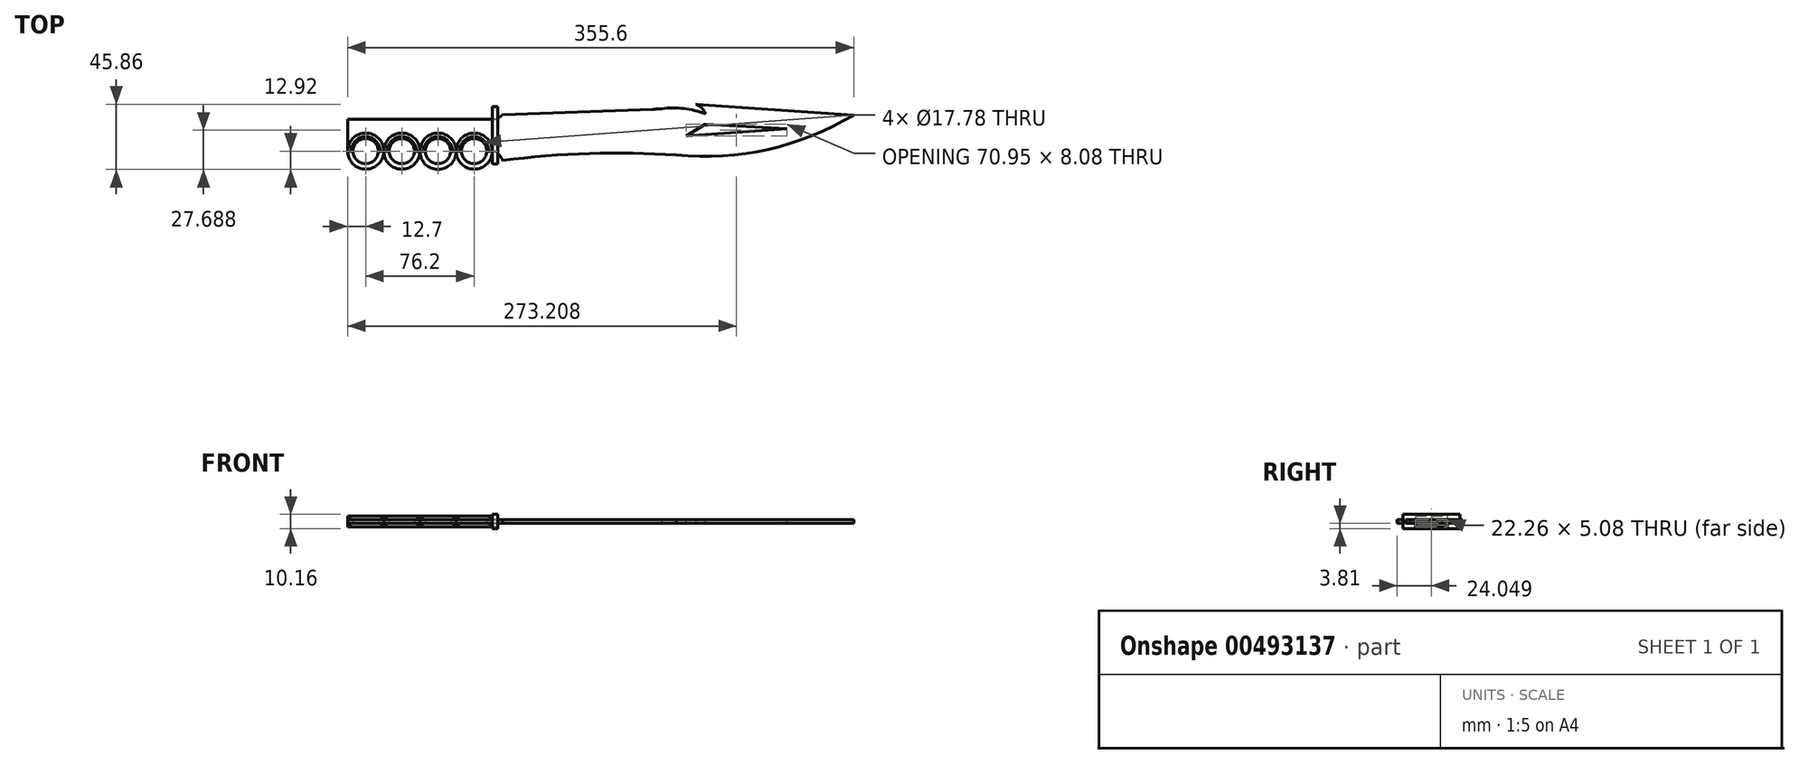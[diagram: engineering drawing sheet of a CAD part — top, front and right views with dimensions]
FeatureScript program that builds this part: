
annotation { "Feature Type Name" : "Feature", "Feature Type Description" : "" }
export const myFeature = defineFeature(function(context is Context, id is Id, definition is map)
    precondition{}
    {
        {
            var Q0;
            Q0=qCreatedBy(makeId("Top.planeOp"),FACE);
            var sketch = newSketch(context, id + "F0", { "sketchPlane" : qUnion([Q0])});
            skLineSegment(sketch, "E0.left", {"start": v(0, 0) * mm, "end": v(0, 22.26) * mm});
            skLineSegment(sketch, "E0.right", {"start": v(-101.6, 0) * mm, "end": v(-101.6, 22.26) * mm});
            skCircle(sketch, "E1", {"center": v(-88.9, 0) * mm, "radius": 8.9 * mm});
            skCircle(sketch, "E2", {"center": v(-63.5, 0) * mm, "radius": 8.9 * mm});
            skCircle(sketch, "E3", {"center": v(-38.1, 0) * mm, "radius": 8.9 * mm});
            skCircle(sketch, "E4", {"center": v(-12.7, 0) * mm, "radius": 8.9 * mm});
            skArc(sketch, "E5", {"start": v(-66.76, 22.26) * mm, "mid": v(-50.8, 21.91) * mm, "end": v(-34.84, 22.26) * mm});
            skPoint(sketch, "E6", {"position": v(-76.2, 0) * mm});
            skPoint(sketch, "E7", {"position": v(-50.8, 0) * mm});
            skPoint(sketch, "E8", {"position": v(-25.4, 0) * mm});
            skArc(sketch, "E9", {"start": v(-101.6, 0) * mm, "mid": v(-88.9, -12.7) * mm, "end": v(-76.2, 0) * mm});
            skArc(sketch, "E10", {"start": v(-76.2, 0) * mm, "mid": v(-63.5, -12.7) * mm, "end": v(-50.8, 0) * mm});
            skArc(sketch, "E11", {"start": v(-50.8, 0) * mm, "mid": v(-38.1, -12.92) * mm, "end": v(-25.4, 0) * mm});
            skPoint(sketch, "E12", {"position": v(-2.71, 7.84) * mm});
            skArc(sketch, "E13", {"start": v(-25.4, 0) * mm, "mid": v(-12.7, -12.7) * mm, "end": v(0, 0) * mm});
            skPoint(sketch, "E14.orphan", {"position": v(-72.39, 0) * mm});
            skPoint(sketch, "E15.trimOffspring.end.orphan", {"position": v(-80.01, 0) * mm});
            skPoint(sketch, "E16.end.orphan", {"position": v(-46.99, 0) * mm});
            skPoint(sketch, "E17.orphan", {"position": v(-54.6, 0) * mm});
            skPoint(sketch, "E18.end.orphan", {"position": v(-21.59, 0) * mm});
            skPoint(sketch, "E19.orphan", {"position": v(-29.2, 0) * mm});
            skLineSegment(sketch, "E20", {"start": v(112.93, 29.45) * mm, "end": v(7.27, 25.66) * mm});
            skPoint(sketch, "E21.orphan", {"position": v(129.42, -2.78) * mm});
            skLineSegment(sketch, "E22", {"start": v(-34.84, 22.26) * mm, "end": v(-101.6, 22.26) * mm});
            skPoint(sketch, "E23.orphan", {"position": v(-101.6, 25.4) * mm});
            skArc(sketch, "E24", {"start": v(7.27, -6.52) * mm, "mid": v(4.54, -2.25) * mm, "end": v(0, 0) * mm});
            skArc(sketch, "E25", {"start": v(129.42, -2.78) * mm, "mid": v(68.26, -1.73) * mm, "end": v(7.27, -6.52) * mm});
            skArc(sketch, "E26", {"start": v(129.42, -2.78) * mm, "mid": v(194, 1.22) * mm, "end": v(254, 25.4) * mm});
            skLineSegment(sketch, "E27", {"start": v(254, 25.4) * mm, "end": v(142.88, 32.94) * mm});
            skArc(sketch, "E28", {"start": v(112.93, 29.45) * mm, "mid": v(116.08, 29.6) * mm, "end": v(119.23, 29.79) * mm});
            skLineSegment(sketch, "E29", {"start": v(-101.6, 0) * mm, "end": v(-21.59, 0) * mm, "construction": true});
            skLineSegment(sketch, "E30.trimOffspring", {"start": v(-3.81, 0) * mm, "end": v(0, 0) * mm, "construction": true});
            skPoint(sketch, "E31.visualSharp", {"position": v(120.84, 29.9) * mm});
            skLineSegment(sketch, "E32", {"start": v(142.88, 32.94) * mm, "end": v(119.23, 29.79) * mm});
            skLineSegment(sketch, "E33", {"start": v(-34.84, 22.26) * mm, "end": v(0, 22.26) * mm});
            skArc(sketch, "E34", {"start": v(0, 22.26) * mm, "mid": v(4.02, 23.15) * mm, "end": v(7.27, 25.66) * mm});
            skPoint(sketch, "E35.orphan", {"position": v(0, 25.4) * mm});
            skSolve(sketch);
        }
        {
            var Q0;
            Q0 = qSketchRegion(id + "F0", true);
            extrude(context, id + "F1", {"entities" : qUnion([Q0]), "depth" : 2.54 * mm});
        }
        {
            var Q0;
            Q0=makeQuery(id+"F1.opExtrude","CAP_FACE",FACE,{"disambiguationData":[OSD([sQuery(id+"F0.wireOp",EDGE,"E0.right"),sQuery(id+"F0.wireOp",EDGE,"E1"),sQuery(id+"F0.wireOp",EDGE,"E2"),sQuery(id+"F0.wireOp",EDGE,"E3"),sQuery(id+"F0.wireOp",EDGE,"E4"),sQuery(id+"F0.wireOp",EDGE,"E9"),sQuery(id+"F0.wireOp",EDGE,"E10"),sQuery(id+"F0.wireOp",EDGE,"E11"),sQuery(id+"F0.wireOp",EDGE,"E13"),sQuery(id+"F0.wireOp",EDGE,"E20"),sQuery(id+"F0.wireOp",EDGE,"E22"),sQuery(id+"F0.wireOp",EDGE,"E24"),sQuery(id+"F0.wireOp",EDGE,"E25"),sQuery(id+"F0.wireOp",EDGE,"E26"),sQuery(id+"F0.wireOp",EDGE,"E27"),sQuery(id+"F0.wireOp",EDGE,"E28"),sQuery(id+"F0.wireOp",EDGE,"E32"),sQuery(id+"F0.wireOp",EDGE,"E33"),sQuery(id+"F0.wireOp",EDGE,"E34")])],"isStart":false});
            var sketch = newSketch(context, id + "F2", { "sketchPlane" : qUnion([Q0])});
            skLineSegment(sketch, "E36", {"start": v(149.48, 18.8) * mm, "end": v(207.09, 15.65) * mm});
            skLineSegment(sketch, "E37", {"start": v(207.09, 15.65) * mm, "end": v(136.13, 10.73) * mm});
            skLineSegment(sketch, "E38", {"start": v(136.13, 10.73) * mm, "end": v(149.48, 18.8) * mm});
            skArc(sketch, "E39", {"start": v(149.83, 26.18) * mm, "mid": v(147.16, 30.39) * mm, "end": v(142.88, 32.94) * mm});
            skArc(sketch, "E40", {"start": v(149.83, 26.18) * mm, "mid": v(134.76, 29.9) * mm, "end": v(119.23, 29.79) * mm});
            skSolve(sketch);
        }
        {
            var Q0;
            Q0=makeQuery(id+"F2.imprint","IMPRINT",FACE,{"disambiguationData":[TD([[makeQuery(id+"F2.imprint","IMPRINT",EDGE,{"derivedFrom":sQuery(id+"F2.wireOp",EDGE,"E39")}),1.0]])]});
            var Q1;
            Q1=makeQuery(id+"F2.imprint","IMPRINT",FACE,{"disambiguationData":[TD([[makeQuery(id+"F2.imprint","IMPRINT",EDGE,{"derivedFrom":sQuery(id+"F2.wireOp",EDGE,"E36")}),-1.0]])]});
            extrude(context, id + "F3", {"entities" : qUnion([Q0, Q1]), "operationType" : NewBodyOperationType.REMOVE, "oppositeDirection" : true, "depth" : 25.4 * mm});
        }
        {
            var Q0;
            Q0=makeQuery(id+"F1.opExtrude","CAP_FACE",FACE,{"disambiguationData":[OSD([sQuery(id+"F0.wireOp",EDGE,"E0.right"),sQuery(id+"F0.wireOp",EDGE,"E1"),sQuery(id+"F0.wireOp",EDGE,"E2"),sQuery(id+"F0.wireOp",EDGE,"E3"),sQuery(id+"F0.wireOp",EDGE,"E4"),sQuery(id+"F0.wireOp",EDGE,"E9"),sQuery(id+"F0.wireOp",EDGE,"E10"),sQuery(id+"F0.wireOp",EDGE,"E11"),sQuery(id+"F0.wireOp",EDGE,"E13"),sQuery(id+"F0.wireOp",EDGE,"E20"),sQuery(id+"F0.wireOp",EDGE,"E22"),sQuery(id+"F0.wireOp",EDGE,"E24"),sQuery(id+"F0.wireOp",EDGE,"E25"),sQuery(id+"F0.wireOp",EDGE,"E26"),sQuery(id+"F0.wireOp",EDGE,"E27"),sQuery(id+"F0.wireOp",EDGE,"E28"),sQuery(id+"F0.wireOp",EDGE,"E32"),sQuery(id+"F0.wireOp",EDGE,"E33"),sQuery(id+"F0.wireOp",EDGE,"E34")])],"isStart":false});
            var sketch = newSketch(context, id + "F4", { "sketchPlane" : qUnion([Q0])});
            skLineSegment(sketch, "E41.0", {"start": v(0, 22.26) * mm, "end": v(-101.6, 22.26) * mm});
            skLineSegment(sketch, "E42.0", {"start": v(-101.6, 0) * mm, "end": v(-101.6, 22.26) * mm});
            skLineSegment(sketch, "E43", {"start": v(-101.6, 0) * mm, "end": v(-97.8, 0) * mm});
            skLineSegment(sketch, "E44", {"start": v(0, 0) * mm, "end": v(0, 22.26) * mm});
            skArc(sketch, "E45.0", {"start": v(-3.81, 0) * mm, "mid": v(-12.7, 8.9) * mm, "end": v(-21.59, 0) * mm});
            skArc(sketch, "E46.0", {"start": v(-29.2, 0) * mm, "mid": v(-38.1, 8.9) * mm, "end": v(-46.99, 0) * mm});
            skArc(sketch, "E47.0", {"start": v(-80.01, 0) * mm, "mid": v(-88.9, 8.89) * mm, "end": v(-97.8, 0) * mm});
            skArc(sketch, "E48.0", {"start": v(-54.6, 0) * mm, "mid": v(-63.5, 8.89) * mm, "end": v(-72.39, 0) * mm});
            skLineSegment(sketch, "E49.trimOffspring", {"start": v(-80.01, 0) * mm, "end": v(-72.39, 0) * mm});
            skLineSegment(sketch, "E50.trimOffspring", {"start": v(-3.81, 0) * mm, "end": v(0, 0) * mm});
            skLineSegment(sketch, "E51.trimOffspring", {"start": v(-54.6, 0) * mm, "end": v(-46.99, 0) * mm});
            skLineSegment(sketch, "E52.trimOffspring", {"start": v(-29.2, 0) * mm, "end": v(-21.59, 0) * mm});
            skSolve(sketch);
        }
        {
            var Q0;
            Q0=makeQuery(id+"F4.imprint","IMPRINT",FACE,{"disambiguationData":[TD([[makeQuery(id+"F4.imprint","IMPRINT",EDGE,{"derivedFrom":sQuery(id+"F4.wireOp",EDGE,"E41.0")}),1.0]])]});
            extrude(context, id + "F5", {"entities" : qUnion([Q0]), "depth" : 2.54 * mm});
        }
        {
            var Q0;
            Q0=makeQuery(id+"F1.opExtrude","CAP_FACE",FACE,{"disambiguationData":[OSD([sQuery(id+"F0.wireOp",EDGE,"E0.right"),sQuery(id+"F0.wireOp",EDGE,"E1"),sQuery(id+"F0.wireOp",EDGE,"E2"),sQuery(id+"F0.wireOp",EDGE,"E3"),sQuery(id+"F0.wireOp",EDGE,"E4"),sQuery(id+"F0.wireOp",EDGE,"E9"),sQuery(id+"F0.wireOp",EDGE,"E10"),sQuery(id+"F0.wireOp",EDGE,"E11"),sQuery(id+"F0.wireOp",EDGE,"E13"),sQuery(id+"F0.wireOp",EDGE,"E20"),sQuery(id+"F0.wireOp",EDGE,"E22"),sQuery(id+"F0.wireOp",EDGE,"E24"),sQuery(id+"F0.wireOp",EDGE,"E25"),sQuery(id+"F0.wireOp",EDGE,"E26"),sQuery(id+"F0.wireOp",EDGE,"E27"),sQuery(id+"F0.wireOp",EDGE,"E28"),sQuery(id+"F0.wireOp",EDGE,"E32"),sQuery(id+"F0.wireOp",EDGE,"E33"),sQuery(id+"F0.wireOp",EDGE,"E34")])],"isStart":true});
            var sketch = newSketch(context, id + "F6", { "sketchPlane" : qUnion([Q0])});
            skLineSegment(sketch, "E53.0", {"start": v(0, -22.26) * mm, "end": v(-101.6, -22.26) * mm});
            skLineSegment(sketch, "E54.0", {"start": v(-101.6, 0) * mm, "end": v(-101.6, -22.26) * mm});
            skLineSegment(sketch, "E55", {"start": v(-101.6, 0) * mm, "end": v(-97.8, 0) * mm});
            skLineSegment(sketch, "E56", {"start": v(0, -22.26) * mm, "end": v(0, 0) * mm});
            skArc(sketch, "E57.0", {"start": v(-97.8, 0) * mm, "mid": v(-88.9, -8.89) * mm, "end": v(-80.01, 0) * mm});
            skArc(sketch, "E58.0", {"start": v(-72.39, 0) * mm, "mid": v(-63.5, -8.89) * mm, "end": v(-54.6, 0) * mm});
            skArc(sketch, "E59.0", {"start": v(-46.99, 0) * mm, "mid": v(-38.1, -8.9) * mm, "end": v(-29.2, 0) * mm});
            skArc(sketch, "E60.0", {"start": v(-21.59, 0) * mm, "mid": v(-12.7, -8.9) * mm, "end": v(-3.81, 0) * mm});
            skLineSegment(sketch, "E61.trimOffspring", {"start": v(-54.6, 0) * mm, "end": v(-46.99, 0) * mm});
            skLineSegment(sketch, "E62.trimOffspring", {"start": v(-80.01, 0) * mm, "end": v(-72.39, 0) * mm});
            skLineSegment(sketch, "E63.trimOffspring", {"start": v(-29.2, 0) * mm, "end": v(-21.59, 0) * mm});
            skLineSegment(sketch, "E64.trimOffspring", {"start": v(-3.81, 0) * mm, "end": v(0, 0) * mm});
            skSolve(sketch);
        }
        {
            var Q0;
            Q0=makeQuery(id+"F6.imprint","IMPRINT",FACE,{"disambiguationData":[TD([[makeQuery(id+"F6.imprint","IMPRINT",EDGE,{"derivedFrom":sQuery(id+"F6.wireOp",EDGE,"E53.0")}),-1.0]])]});
            extrude(context, id + "F7", {"entities" : qUnion([Q0]), "depth" : 2.54 * mm});
        }
        {
            var Q0;
            Q0=makeQuery(id+"F5.opExtrude","CAP_EDGE",EDGE,{"disambiguationData":[OSD([sQuery(id+"F4.wireOp",EDGE,"E47.0")])],"isStart":false});
            var Q1;
            Q1=makeQuery(id+"F5.opExtrude","CAP_EDGE",EDGE,{"disambiguationData":[OSD([sQuery(id+"F4.wireOp",EDGE,"E48.0")])],"isStart":false});
            var Q2;
            Q2=makeQuery(id+"F5.opExtrude","CAP_EDGE",EDGE,{"disambiguationData":[OSD([sQuery(id+"F4.wireOp",EDGE,"E46.0")])],"isStart":false});
            var Q3;
            Q3=makeQuery(id+"F5.opExtrude","CAP_EDGE",EDGE,{"disambiguationData":[OSD([sQuery(id+"F4.wireOp",EDGE,"E45.0")])],"isStart":false});
            var Q4;
            Q4=makeQuery(id+"F7.opExtrude","CAP_EDGE",EDGE,{"disambiguationData":[OSD([sQuery(id+"F6.wireOp",EDGE,"E59.0")])],"isStart":false});
            var Q5;
            Q5=makeQuery(id+"F7.opExtrude","CAP_EDGE",EDGE,{"disambiguationData":[OSD([sQuery(id+"F6.wireOp",EDGE,"E60.0")])],"isStart":false});
            var Q6;
            Q6=makeQuery(id+"F7.opExtrude","CAP_EDGE",EDGE,{"disambiguationData":[OSD([sQuery(id+"F6.wireOp",EDGE,"E58.0")])],"isStart":false});
            var Q7;
            Q7=makeQuery(id+"F7.opExtrude","CAP_EDGE",EDGE,{"disambiguationData":[OSD([sQuery(id+"F6.wireOp",EDGE,"E57.0")])],"isStart":false});
            chamfer(context, id + "F8", {"entities" : qUnion([Q0, Q1, Q2, Q3, Q4, Q5, Q6, Q7]), "width" : 3.8 * mm, "tangentPropagation" : true});
        }
        {
            var Q0;
            Q0=makeQuery(id+"F7.opExtrude","SWEPT_FACE",FACE,{"disambiguationData":[OSD([sQuery(id+"F6.wireOp",EDGE,"E56")])]});
            var sketch = newSketch(context, id + "F9", { "sketchPlane" : qUnion([Q0])});
            skLineSegment(sketch, "E65.0", {"start": v(22.26, 0) * mm, "end": v(0, 0) * mm});
            skLineSegment(sketch, "E66.0", {"start": v(0, 2.54) * mm, "end": v(0, 0) * mm});
            skLineSegment(sketch, "E67.0", {"start": v(22.26, 2.54) * mm, "end": v(22.26, 0) * mm});
            skLineSegment(sketch, "E68.0", {"start": v(0, 2.54) * mm, "end": v(22.26, 2.54) * mm});
            skLineSegment(sketch, "E69.0", {"start": v(22.26, -3.81) * mm, "end": v(0, -3.81) * mm});
            skLineSegment(sketch, "E70.0", {"start": v(0, 6.35) * mm, "end": v(22.26, 6.35) * mm});
            skLineSegment(sketch, "E71", {"start": v(0, 6.35) * mm, "end": v(-8.89, 6.35) * mm});
            skLineSegment(sketch, "E72", {"start": v(0, -3.81) * mm, "end": v(-8.89, -3.81) * mm});
            skLineSegment(sketch, "E73", {"start": v(-8.89, -3.81) * mm, "end": v(-8.89, 6.35) * mm});
            skPoint(sketch, "E74", {"position": v(22.26, 2.54) * mm});
            skPoint(sketch, "E75", {"position": v(22.26, 0) * mm});
            skPoint(sketch, "E76.orphan", {"position": v(22.26, -3.81) * mm});
            skPoint(sketch, "E77.startSnap0", {"position": v(22.26, -1.27) * mm});
            skLineSegment(sketch, "E78", {"start": v(31.15, 6.35) * mm, "end": v(31.15, -3.81) * mm});
            skPoint(sketch, "E79.orphan", {"position": v(22.26, 6.35) * mm});
            skLineSegment(sketch, "E80", {"start": v(22.26, 6.35) * mm, "end": v(31.15, 6.35) * mm});
            skLineSegment(sketch, "E81", {"start": v(22.26, -3.81) * mm, "end": v(31.15, -3.81) * mm});
            skSolve(sketch);
        }
        {
            var Q0;
            Q0=makeQuery(id+"F9.imprint","IMPRINT",FACE,{"disambiguationData":[TD([[makeQuery(id+"F9.imprint","IMPRINT",EDGE,{"derivedFrom":sQuery(id+"F9.wireOp",EDGE,"E66.0")}),-1.0]])]});
            extrude(context, id + "F10", {"entities" : qUnion([Q0]), "depth" : 3.8 * mm});
        }
    });
